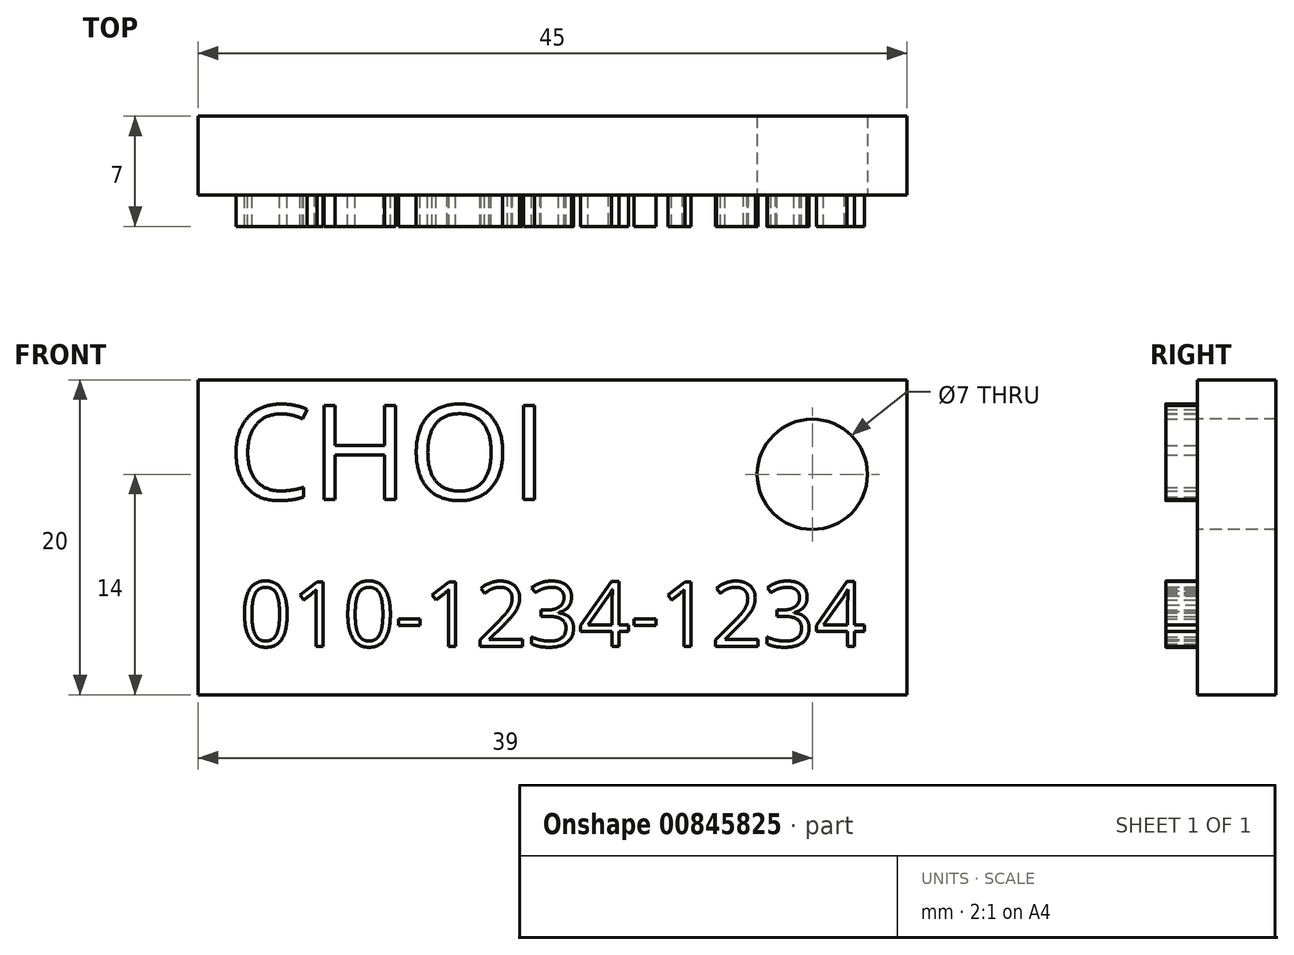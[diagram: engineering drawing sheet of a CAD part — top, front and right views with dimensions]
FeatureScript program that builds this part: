
annotation { "Feature Type Name" : "Feature", "Feature Type Description" : "" }
export const myFeature = defineFeature(function(context is Context, id is Id, definition is map)
    precondition{}
    {
        {
            var Q0;
            Q0=qCreatedBy(makeId("Front.planeOp"),FACE);
            var sketch = newSketch(context, id + "F0", { "sketchPlane" : qUnion([Q0])});
            skLineSegment(sketch, "E0.bottom", {"start": v(0, 0) * mm, "end": v(45, 0) * mm});
            skLineSegment(sketch, "E0.top", {"start": v(0, 20) * mm, "end": v(45, 20) * mm});
            skLineSegment(sketch, "E0.left", {"start": v(0, 0) * mm, "end": v(0, 20) * mm});
            skLineSegment(sketch, "E0.right", {"start": v(45, 0) * mm, "end": v(45, 20) * mm});
            skSolve(sketch);
        }
        {
            var Q0;
            Q0=makeQuery(id+"F0.imprint","IMPRINT",FACE,{"disambiguationData":[TD([[makeQuery(id+"F0.imprint","IMPRINT",EDGE,{"derivedFrom":sQuery(id+"F0.wireOp",EDGE,"E0.bottom")}),1.0]])]});
            extrude(context, id + "F1", {"entities" : qUnion([Q0]), "depth" : 5 * mm, "offsetDistance" : 25 * mm});
        }
        {
            var Q0;
            Q0=makeQuery(id+"F1.opExtrude","CAP_FACE",FACE,{"disambiguationData":[OSD([sQuery(id+"F0.wireOp",EDGE,"E0.bottom"),sQuery(id+"F0.wireOp",EDGE,"E0.top"),sQuery(id+"F0.wireOp",EDGE,"E0.left"),sQuery(id+"F0.wireOp",EDGE,"E0.right")])],"isStart":false});
            var sketch = newSketch(context, id + "F2", { "sketchPlane" : qUnion([Q0])});
            skText(sketch, "E1", { "text": "CHOI", "fontName": "OpenSans-Regular.ttf"});
            const initialGuessF2  = {"E1": [0.00189, 0.01241, 1, 0, 0.00602]};
            skSetInitialGuess(sketch, initialGuessF2);
            skSolve(sketch);
        }
        {
            var Q0;
            Q0 = qSketchRegion(id + "F2", true);
            extrude(context, id + "F3", {"entities" : qUnion([Q0]), "operationType" : NewBodyOperationType.ADD, "depth" : 2 * mm, "offsetDistance" : 25 * mm});
        }
        {
            var Q0;
            {var subQ0=sQuery(id+"F0.wireOp",EDGE,"E0.top");var subQ1=sQuery(id+"F0.wireOp",EDGE,"E0.right");var subQ2=sQuery(id+"F0.wireOp",EDGE,"E0.bottom");var subQ3=sQuery(id+"F0.wireOp",EDGE,"E0.left");Q0=makeQuery(id+"F3.boolean.opBoolean","SPLIT",FACE,{"disambiguationData":[TD([makeQuery(id+"F1.opExtrude","SWEPT_FACE",FACE,{"disambiguationData":[OSD([subQ2])]})])],"derivedFrom":makeQuery(id+"F1.opExtrude","CAP_FACE",FACE,{"disambiguationData":[OSD([subQ2,subQ0,subQ3,subQ1])],"isStart":false})});}
            var sketch = newSketch(context, id + "F4", { "sketchPlane" : qUnion([Q0])});
            skText(sketch, "E2", { "text": "010-1234-1234", "fontName": "OpenSans-Regular.ttf"});
            const initialGuessF4  = {"E2": [0.00265, 0.00307, 1, 0, 0.00413]};
            skSetInitialGuess(sketch, initialGuessF4);
            skSolve(sketch);
        }
        {
            var Q0;
            Q0 = qSketchRegion(id + "F4", true);
            extrude(context, id + "F5", {"entities" : qUnion([Q0]), "operationType" : NewBodyOperationType.ADD, "depth" : 2 * mm, "offsetDistance" : 25 * mm});
        }
        {
            var Q0;
            {var subQ29=sQuery(id+"F0.wireOp",EDGE,"E0.top");var subQ37=sQuery(id+"F0.wireOp",EDGE,"E0.left");var subQ39=sQuery(id+"F0.wireOp",EDGE,"E0.bottom");var subQ40=makeQuery(id+"F1.opExtrude","SWEPT_FACE",FACE,{"disambiguationData":[OSD([subQ39])]});var subQ42=sQuery(id+"F0.wireOp",EDGE,"E0.right");Q0=makeQuery(id+"F5.boolean.opBoolean","SPLIT",FACE,{"disambiguationData":[TD([subQ40])],"derivedFrom":makeQuery(id+"F3.boolean.opBoolean","SPLIT",FACE,{"disambiguationData":[TD([subQ40])],"derivedFrom":makeQuery(id+"F1.opExtrude","CAP_FACE",FACE,{"disambiguationData":[OSD([subQ39,subQ29,subQ37,subQ42])],"isStart":false})})});}
            var sketch = newSketch(context, id + "F6", { "sketchPlane" : qUnion([Q0])});
            skCircle(sketch, "E3", {"center": v(39, 14) * mm, "radius": 3.5 * mm});
            skSolve(sketch);
        }
        {
            var Q0;
            Q0=makeQuery(id+"F6.imprint","IMPRINT",FACE,{"disambiguationData":[TD([[makeQuery(id+"F6.imprint","IMPRINT",EDGE,{"derivedFrom":sQuery(id+"F6.wireOp",EDGE,"E3")}),1.0]])]});
            extrude(context, id + "F7", {"entities" : qUnion([Q0]), "operationType" : NewBodyOperationType.REMOVE, "oppositeDirection" : true, "depth" : 5 * mm, "offsetDistance" : 25 * mm});
        }
    });
